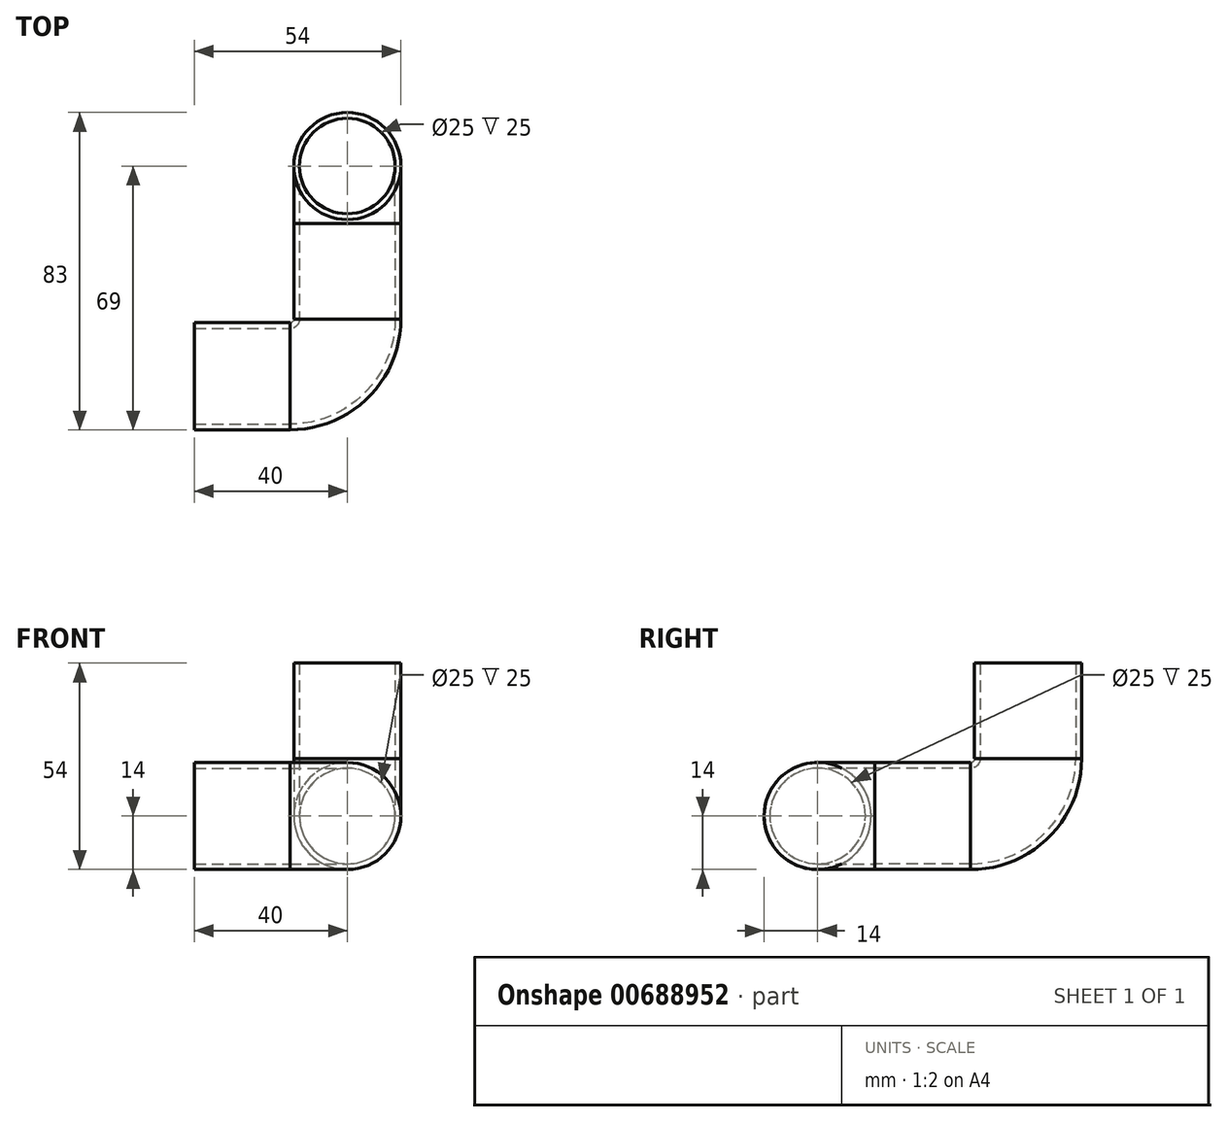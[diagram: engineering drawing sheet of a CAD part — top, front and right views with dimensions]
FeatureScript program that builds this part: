
annotation { "Feature Type Name" : "Feature", "Feature Type Description" : "" }
export const myFeature = defineFeature(function(context is Context, id is Id, definition is map)
    precondition{}
    {
        {
            var Q0;
            Q0=qCreatedBy(makeId("Top.planeOp"),FACE);
            var sketch = newSketch(context, id + "F0", { "sketchPlane" : qUnion([Q0])});
            skLineSegment(sketch, "E0", {"start": v(0, 0) * mm, "end": v(-40, 0) * mm});
            skLineSegment(sketch, "E1", {"start": v(-40, 0) * mm, "end": v(-40, 12.5) * mm, "construction": true});
            skLineSegment(sketch, "E2", {"start": v(-40, 12.5) * mm, "end": v(-40, 14) * mm, "construction": true});
            skLineSegment(sketch, "E3.bottom", {"start": v(-40, 12.5) * mm, "end": v(-15, 12.5) * mm});
            skLineSegment(sketch, "E3.top", {"start": v(-40, 14) * mm, "end": v(-15, 14) * mm});
            skLineSegment(sketch, "E3.left", {"start": v(-40, 12.5) * mm, "end": v(-40, 14) * mm});
            skLineSegment(sketch, "E3.right", {"start": v(-15, 12.5) * mm, "end": v(-15, 14) * mm});
            skLineSegment(sketch, "E4.bottom", {"start": v(0, 0) * mm, "end": v(-15, 0) * mm, "construction": true});
            skLineSegment(sketch, "E4.top", {"start": v(0, 15) * mm, "end": v(-15, 15) * mm, "construction": true});
            skLineSegment(sketch, "E4.left", {"start": v(0, 0) * mm, "end": v(0, 15) * mm, "construction": true});
            skLineSegment(sketch, "E4.right", {"start": v(-15, 0) * mm, "end": v(-15, 15) * mm, "construction": true});
            skArc(sketch, "E5", {"start": v(-15, 0) * mm, "mid": v(0, 0) * mm, "end": v(0, 15) * mm});
            skSolve(sketch);
        }
        {
            var Q0;
            Q0=qCreatedBy(makeId("Top.planeOp"),FACE);
            var sketch = newSketch(context, id + "F1", { "sketchPlane" : qUnion([Q0])});
            skLineSegment(sketch, "E6", {"start": v(0, 0) * mm, "end": v(0, 49) * mm});
            skLineSegment(sketch, "E7", {"start": v(0, 0) * mm, "end": v(14, 0) * mm, "construction": true});
            skLineSegment(sketch, "E8", {"start": v(14, 15) * mm, "end": v(14, 0) * mm, "construction": true});
            skLineSegment(sketch, "E9.bottom", {"start": v(14, 15) * mm, "end": v(12.5, 15) * mm});
            skLineSegment(sketch, "E9.top", {"start": v(14, 40) * mm, "end": v(12.5, 40) * mm});
            skLineSegment(sketch, "E9.left", {"start": v(14, 15) * mm, "end": v(14, 40) * mm});
            skLineSegment(sketch, "E9.right", {"start": v(12.5, 15) * mm, "end": v(12.5, 40) * mm});
            skLineSegment(sketch, "E10", {"start": v(14, 15) * mm, "end": v(12.5, 15) * mm, "construction": true});
            skSolve(sketch);
        }
        {
            var Q0;
            Q0=qCreatedBy(makeId("Right.planeOp"),FACE);
            var sketch = newSketch(context, id + "F2", { "sketchPlane" : qUnion([Q0])});
            skLineSegment(sketch, "E11", {"start": v(55, 0) * mm, "end": v(55, 40) * mm});
            skLineSegment(sketch, "E12", {"start": v(0, 0) * mm, "end": v(55, 0) * mm, "construction": true});
            skLineSegment(sketch, "E13", {"start": v(55, 40) * mm, "end": v(42.5, 40) * mm, "construction": true});
            skLineSegment(sketch, "E14.bottom", {"start": v(42.5, 40) * mm, "end": v(41, 40) * mm});
            skLineSegment(sketch, "E14.top", {"start": v(42.5, 15) * mm, "end": v(41, 15) * mm});
            skLineSegment(sketch, "E14.left", {"start": v(42.5, 40) * mm, "end": v(42.5, 15) * mm});
            skLineSegment(sketch, "E14.right", {"start": v(41, 40) * mm, "end": v(41, 15) * mm});
            skLineSegment(sketch, "E15", {"start": v(41, 15) * mm, "end": v(41, 0) * mm});
            skSolve(sketch);
        }
        {
            var Q0;
            Q0=makeQuery(id+"F0.imprint","IMPRINT",FACE,{"disambiguationData":[TD([[makeQuery(id+"F0.imprint","IMPRINT",EDGE,{"derivedFrom":sQuery(id+"F0.wireOp",EDGE,"E3.bottom")}),1.0]])]});
            var Q1;
            Q1=sQuery(id+"F0.wireOp",EDGE,"E0");
            revolve(context, id + "F3", {"entities" : qUnion([Q0]), "axis" : qUnion([Q1]), "revolveType" : RevolveType.FULL});
        }
        {
            var Q0;
            Q0=makeQuery(id+"F1.imprint","IMPRINT",FACE,{"disambiguationData":[TD([[makeQuery(id+"F1.imprint","IMPRINT",EDGE,{"derivedFrom":sQuery(id+"F1.wireOp",EDGE,"E9.bottom")}),-1.0]])]});
            var Q1;
            Q1=sQuery(id+"F1.wireOp",EDGE,"E6");
            revolve(context, id + "F4", {"operationType" : NewBodyOperationType.ADD, "entities" : qUnion([Q0]), "axis" : qUnion([Q1]), "revolveType" : RevolveType.FULL});
        }
        {
            var Q0;
            Q0=makeQuery(id+"F2.imprint","IMPRINT",FACE,{"disambiguationData":[TD([[makeQuery(id+"F2.imprint","IMPRINT",EDGE,{"derivedFrom":sQuery(id+"F2.wireOp",EDGE,"E14.bottom")}),1.0]])]});
            var Q1;
            Q1=sQuery(id+"F2.wireOp",EDGE,"E11");
            revolve(context, id + "F5", {"operationType" : NewBodyOperationType.ADD, "entities" : qUnion([Q0]), "axis" : qUnion([Q1]), "revolveType" : RevolveType.FULL});
        }
        {
            var Q0;
            Q0=qCreatedBy(makeId("Top.planeOp"),FACE);
            var sketch = newSketch(context, id + "F6", { "sketchPlane" : qUnion([Q0])});
            skArc(sketch, "E16", {"start": v(-15, 0) * mm, "mid": v(-4.4, 4.4) * mm, "end": v(0, 15) * mm});
            skLineSegment(sketch, "E17", {"start": v(-15, 0) * mm, "end": v(0, 0) * mm, "construction": true});
            skLineSegment(sketch, "E18", {"start": v(0, 0) * mm, "end": v(0, 15) * mm, "construction": true});
            skLineSegment(sketch, "E19", {"start": v(-15, 15) * mm, "end": v(-4.4, 4.4) * mm, "construction": true});
            skSolve(sketch);
        }
        {
            var Q0;
            Q0=makeQuery(id+"F4.opRevolve","SWEPT_FACE",FACE,{"disambiguationData":[OSD([sQuery(id+"F1.wireOp",EDGE,"E9.bottom")])]});
            var Q1;
            Q1=makeQuery(id+"F3.opRevolve","SWEPT_FACE",FACE,{"disambiguationData":[OSD([sQuery(id+"F0.wireOp",EDGE,"E3.right")])]});
            var Q2;
            Q2=sQuery(id+"F6.wireOp",EDGE,"E16");
            sweep(context, id + "F7", {"profiles" : qUnion([Q0, Q1]), "path" : qUnion([Q2])});
        }
        {
            var Q0;
            Q0=qCreatedBy(makeId("Right.planeOp"),FACE);
            var sketch = newSketch(context, id + "F8", { "sketchPlane" : qUnion([Q0])});
            skLineSegment(sketch, "E20", {"start": v(0, 0) * mm, "end": v(40, 0) * mm, "construction": true});
            skLineSegment(sketch, "E21", {"start": v(40, 0) * mm, "end": v(55, 0) * mm, "construction": true});
            skLineSegment(sketch, "E22", {"start": v(55, 0) * mm, "end": v(55, 15) * mm, "construction": true});
            skArc(sketch, "E23", {"start": v(40, 0) * mm, "mid": v(50.6, 4.4) * mm, "end": v(55, 15) * mm});
            skSolve(sketch);
        }
        {
            var Q0;
            Q0=makeQuery(id+"F4.opRevolve","SWEPT_FACE",FACE,{"disambiguationData":[OSD([sQuery(id+"F1.wireOp",EDGE,"E9.top")])]});
            var Q1;
            Q1=makeQuery(id+"F5.opRevolve","SWEPT_FACE",FACE,{"disambiguationData":[OSD([sQuery(id+"F2.wireOp",EDGE,"E14.top")])]});
            var Q2;
            Q2=sQuery(id+"F8.wireOp",EDGE,"E23");
            sweep(context, id + "F9", {"profiles" : qUnion([Q0, Q1]), "path" : qUnion([Q2])});
        }
    });
